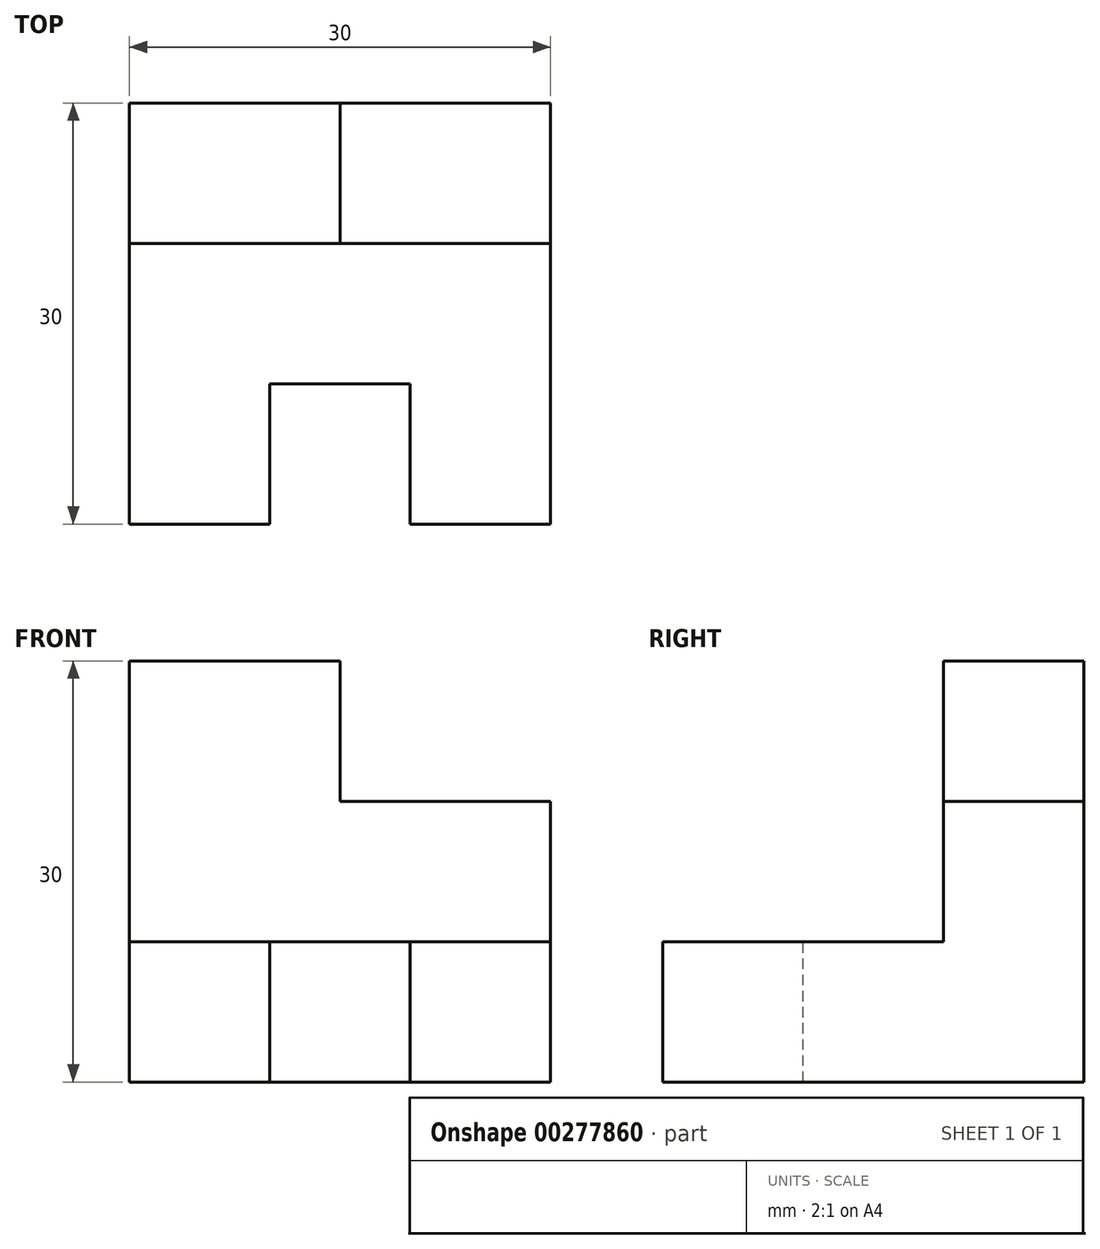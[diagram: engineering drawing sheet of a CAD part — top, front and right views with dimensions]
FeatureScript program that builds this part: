
annotation { "Feature Type Name" : "Feature", "Feature Type Description" : "" }
export const myFeature = defineFeature(function(context is Context, id is Id, definition is map)
    precondition{}
    {
        {
            var Q0;
            Q0=qCreatedBy(makeId("Right.planeOp"),FACE);
            var sketch = newSketch(context, id + "F0", { "sketchPlane" : qUnion([Q0])});
            skLineSegment(sketch, "E0.bottom", {"start": v(0, 0) * mm, "end": v(30, 0) * mm});
            skLineSegment(sketch, "E0.top", {"start": v(0, 30) * mm, "end": v(30, 30) * mm});
            skLineSegment(sketch, "E0.left", {"start": v(0, 0) * mm, "end": v(0, 30) * mm});
            skLineSegment(sketch, "E0.right", {"start": v(30, 0) * mm, "end": v(30, 30) * mm});
            skLineSegment(sketch, "E1", {"start": v(0, 10) * mm, "end": v(20, 10) * mm});
            skLineSegment(sketch, "E2", {"start": v(20, 10) * mm, "end": v(20, 30) * mm});
            skSolve(sketch);
        }
        {
            var Q0;
            {var subQ2=sQuery(id+"F0.wireOp",EDGE,"E0.bottom");Q0=makeQuery(id+"F0.imprint","IMPRINT",FACE,{"disambiguationData":[TD([[makeQuery(id+"F0.imprint","IMPRINT",EDGE,{"derivedFrom":subQ2}),1.0]])]});}
            extrude(context, id + "F1", {"entities" : qUnion([Q0]), "depth" : 30 * mm});
        }
        {
            var Q0;
            Q0=makeQuery(id+"F1.opExtrude","SWEPT_FACE",FACE,{"disambiguationData":[OSD([sQuery(id+"F0.wireOp",EDGE,"E1")])]});
            var sketch = newSketch(context, id + "F2", { "sketchPlane" : qUnion([Q0])});
            skLineSegment(sketch, "E3.bottom", {"start": v(10, 0) * mm, "end": v(20, 0) * mm});
            skLineSegment(sketch, "E3.top", {"start": v(10, 10) * mm, "end": v(20, 10) * mm});
            skLineSegment(sketch, "E3.left", {"start": v(10, 0) * mm, "end": v(10, 10) * mm});
            skLineSegment(sketch, "E3.right", {"start": v(20, 0) * mm, "end": v(20, 10) * mm});
            skSolve(sketch);
        }
        {
            var Q0;
            Q0 = qSketchRegion(id + "F2", true);
            extrude(context, id + "F3", {"entities" : qUnion([Q0]), "operationType" : NewBodyOperationType.REMOVE, "endBound" : BoundingType.THROUGH_ALL, "oppositeDirection" : true, "depth" : 25 * mm});
        }
        {
            var Q0;
            Q0=makeQuery(id+"F1.opExtrude","SWEPT_FACE",FACE,{"disambiguationData":[OSD([sQuery(id+"F0.wireOp",EDGE,"E2")])]});
            var sketch = newSketch(context, id + "F4", { "sketchPlane" : qUnion([Q0])});
            skPoint(sketch, "E4.oppositeSnap0", {"position": v(15, 30) * mm});
            skLineSegment(sketch, "E4.bottom", {"start": v(30, 30) * mm, "end": v(15, 30) * mm});
            skLineSegment(sketch, "E4.top", {"start": v(30, 20) * mm, "end": v(15, 20) * mm});
            skLineSegment(sketch, "E4.left", {"start": v(30, 30) * mm, "end": v(30, 20) * mm});
            skLineSegment(sketch, "E4.right", {"start": v(15, 30) * mm, "end": v(15, 20) * mm});
            skSolve(sketch);
        }
        {
            var Q0;
            Q0 = qSketchRegion(id + "F4", true);
            extrude(context, id + "F5", {"entities" : qUnion([Q0]), "operationType" : NewBodyOperationType.REMOVE, "endBound" : BoundingType.THROUGH_ALL, "oppositeDirection" : true, "depth" : 25 * mm});
        }
    });
